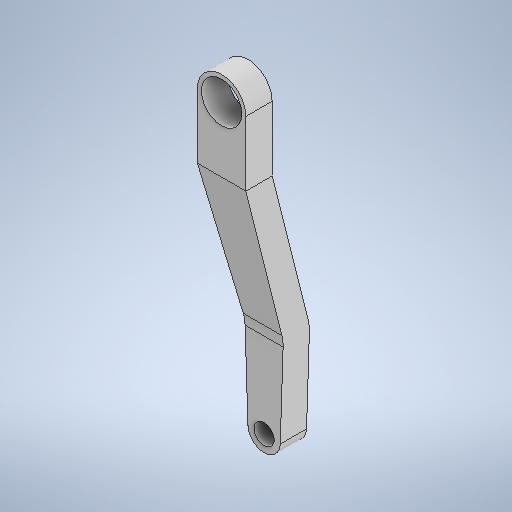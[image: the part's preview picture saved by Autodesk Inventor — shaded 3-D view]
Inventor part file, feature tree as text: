
AUTODESK INVENTOR PART (.ipt)
format: ipt  version: 2025.1 (Build 291241000, 241)  size: 315,392 bytes
history: native  units: mm
features: sketch x5, extrude x3, hole x2, fillet x1, projected_geometry x1
ambient origin geometry x8: Origin, YZ Plane, XZ Plane, XY Plane, X Axis, Y Axis, Z Axis, Center Point
bodies: Body1 (feature_tree)
feature tree (12):
  extrude  "Extrusion7"  Depth=10.0mm
  extrude  "Extrusion8"  Depth=10.5mm
  extrude  "Extrusion9"  Depth=22.0mm
  hole  "Hole1"  [1 undecoded]
  hole  "Hole2"  [1 undecoded]
  fillet  "Fillet1"  Radius=8.0mm
  sketch  "Sketch19"  dims[d79=10.0mm d80=10.0mm]
  sketch  "Sketch20"  dims[d82=6.5mm d83=10.5mm]
  sketch  "Sketch21"  dims[d84=25.0mm d85=22.0mm]
  projected_geometry  "Projected Loop13"
  sketch  "Sketch22"  dims[d86=37.940206mm d87=12.0mm d88=0.0mm]
  sketch  "Sketch23"  dims[d89=12.0mm d90=12.0mm d91=0.0mm d93=8.0mm d94=12.0mm d95=0.0mm d96=10.0mm d97=6.0mm d98=4.0mm d99=2.0mm d100=90.0deg d101=8.0mm d102=20.594885mm d103=5.0mm d104=6.0mm d105=4.0mm d106=2.0mm d107=90.0deg d108=8.0mm d109=20.594885mm d110=10.0mm d92=0.0mm]
note: 2 required parameter values undecoded (feature->parameter linkage not recoverable at this tier; creation-order binding heuristic only, values carry confidence <= 0.55)
